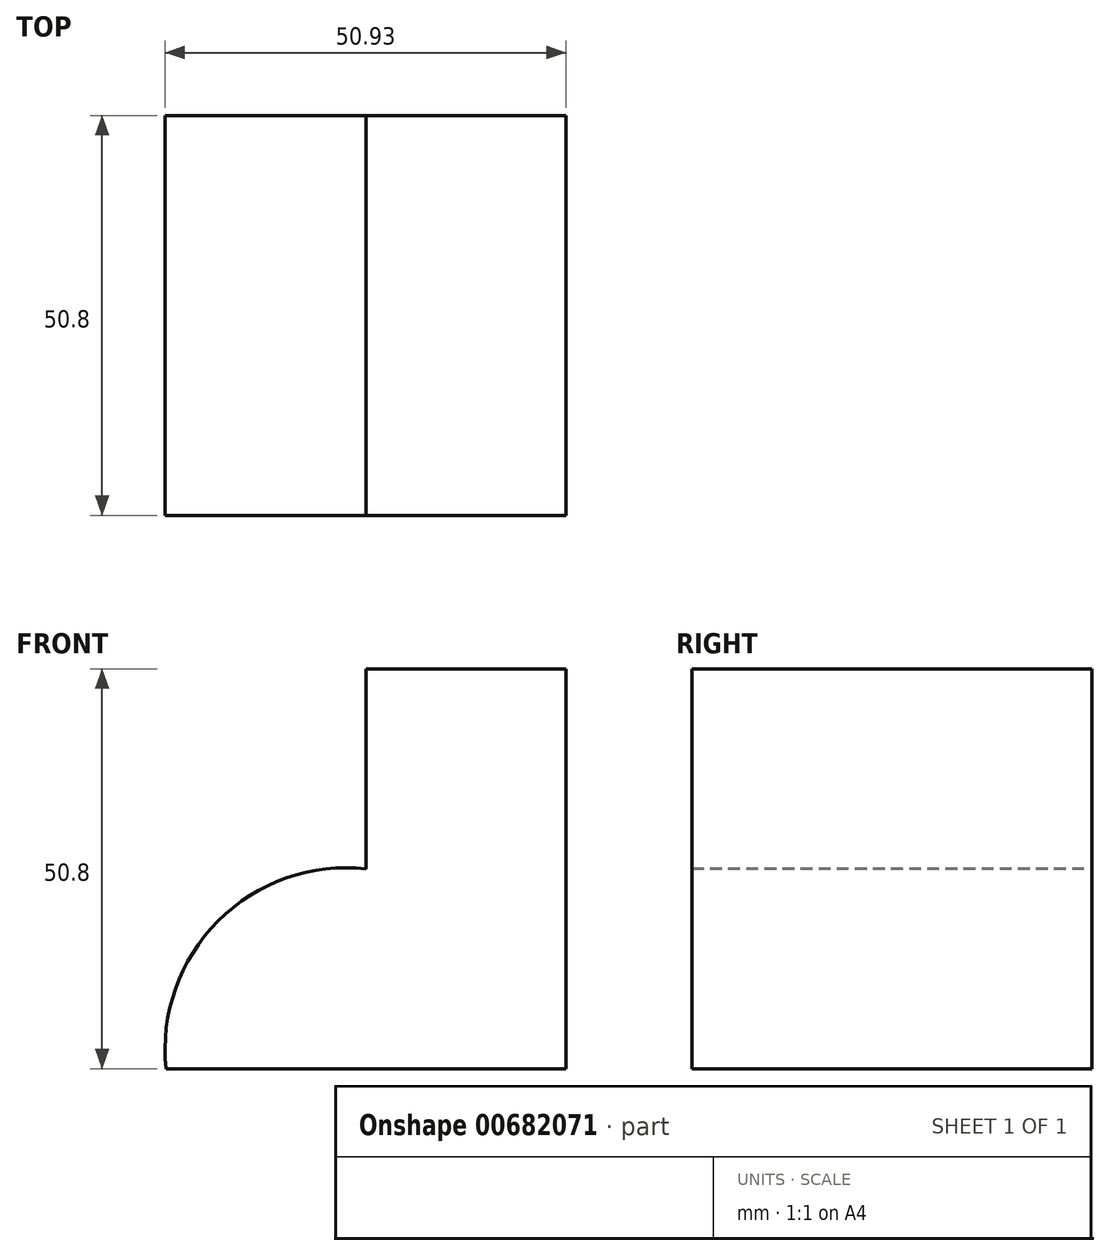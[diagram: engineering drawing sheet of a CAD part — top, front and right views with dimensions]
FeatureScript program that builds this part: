
annotation { "Feature Type Name" : "Feature", "Feature Type Description" : "" }
export const myFeature = defineFeature(function(context is Context, id is Id, definition is map)
    precondition{}
    {
        {
            var Q0;
            Q0=qCreatedBy(makeId("Front.planeOp"),FACE);
            var sketch = newSketch(context, id + "F0", { "sketchPlane" : qUnion([Q0])});
            skLineSegment(sketch, "E0", {"start": v(0, 0) * mm, "end": v(-50.8, 0) * mm});
            skLineSegment(sketch, "E1", {"start": v(0, 0) * mm, "end": v(0, 50.8) * mm});
            skLineSegment(sketch, "E2", {"start": v(0, 50.8) * mm, "end": v(-25.4, 50.8) * mm});
            skLineSegment(sketch, "E3", {"start": v(-25.4, 50.8) * mm, "end": v(-25.4, 25.4) * mm});
            skArc(sketch, "E4", {"start": v(-25.4, 25.4) * mm, "mid": v(-44.17, 18.77) * mm, "end": v(-50.8, 0) * mm});
            skSolve(sketch);
        }
        {
            var Q0;
            Q0 = qSketchRegion(id + "F0", true);
            extrude(context, id + "F1", {"entities" : qUnion([Q0]), "depth" : 50.8 * mm, "offsetDistance" : 25.4 * mm});
        }
    });
